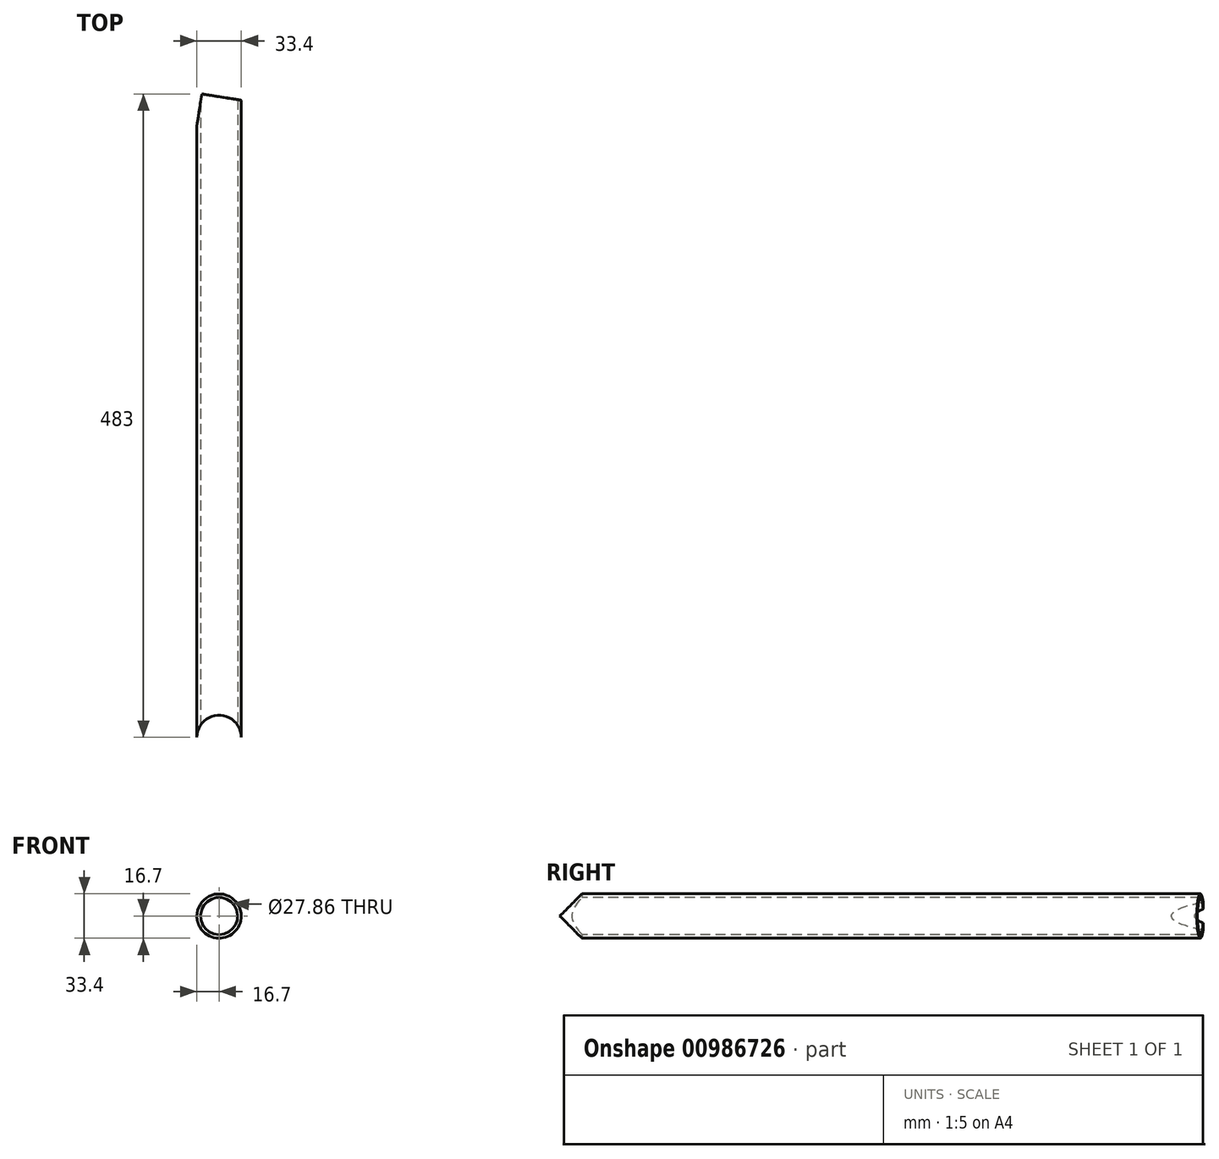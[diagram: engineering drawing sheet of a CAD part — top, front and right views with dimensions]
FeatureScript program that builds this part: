
annotation { "Feature Type Name" : "Feature", "Feature Type Description" : "" }
export const myFeature = defineFeature(function(context is Context, id is Id, definition is map)
    precondition{}
    {
        {
            var Q0;
            Q0=qCreatedBy(makeId("Right.planeOp"),FACE);
            var sketch = newSketch(context, id + "F0", { "sketchPlane" : qUnion([Q0])});
            skLineSegment(sketch, "E0", {"start": v(0, 0) * mm, "end": v(-483.6, 0) * mm});
            skPoint(sketch, "E1.visualSharp", {"position": v(-483.6, 0) * mm});
            skSolve(sketch);
        }
        {
            var Q0;
            Q0=qCreatedBy(makeId("Front.planeOp"),FACE);
            var sketch = newSketch(context, id + "F1", { "sketchPlane" : qUnion([Q0])});
            skCircle(sketch, "E2", {"center": v(0, 0) * mm, "radius": 16.7 * mm});
            skCircle(sketch, "E3.0", {"center": v(0, 0) * mm, "radius": 13.93 * mm});
            skSolve(sketch);
        }
        {
            var Q0;
            Q0=makeQuery(id+"F1.imprint","IMPRINT",FACE,{"disambiguationData":[TD([[makeQuery(id+"F1.imprint","IMPRINT",EDGE,{"derivedFrom":sQuery(id+"F1.wireOp",EDGE,"E2")}),1.0]])]});
            var Q1;
            Q1=sQuery(id+"F0.wireOp",EDGE,"E0");
            var Q2;
            Q2=sQuery(id+"F0.wireOp",EDGE,"E1.filletArc");
            var Q3;
            Q3=sQuery(id+"F0.wireOp",EDGE,"YA7wz6Jj-Of4G-qhnx-SV3L-edTmK6ZEOY0Y");
            sweep(context, id + "F2", {"profiles" : qUnion([Q0]), "path" : qUnion([Q1, Q2, Q3])});
        }
        {
            var Q0;
            Q0=qCreatedBy(makeId("Top.planeOp"),FACE);
            var sketch = newSketch(context, id + "F3", { "sketchPlane" : qUnion([Q0])});
            skLineSegment(sketch, "E4", {"start": v(0, 0) * mm, "end": v(29.63, -4.7) * mm});
            skLineSegment(sketch, "E5", {"start": v(0, 0) * mm, "end": v(16.7, 0) * mm});
            skLineSegment(sketch, "E6", {"start": v(16.7, 0) * mm, "end": v(16.7, -2.65) * mm});
            skLineSegment(sketch, "E7", {"start": v(0, 0) * mm, "end": v(2.57, 16.22) * mm});
            skLineSegment(sketch, "E8.MirrorCS", {"start": v(0, 0) * mm, "end": v(-29.63, 4.7) * mm});
            skLineSegment(sketch, "E9.MirrorCS", {"start": v(-15.88, 5.16) * mm, "end": v(-16.7, 2.65) * mm});
            skLineSegment(sketch, "E10", {"start": v(-16.7, 2.65) * mm, "end": v(-16.7, 0) * mm});
            skLineSegment(sketch, "E11", {"start": v(-16.7, 0) * mm, "end": v(17.86, -5.47) * mm});
            skLineSegment(sketch, "E12", {"start": v(-16.7, 0) * mm, "end": v(16.7, 0) * mm});
            skLineSegment(sketch, "E13", {"start": v(16.7, -5.47) * mm, "end": v(16.7, 0) * mm});
            skLineSegment(sketch, "E14", {"start": v(0, 0) * mm, "end": v(-16.7, 0) * mm});
            skLineSegment(sketch, "E15", {"start": v(-16.7, 0) * mm, "end": v(0, 0) * mm});
            skLineSegment(sketch, "E16", {"start": v(16.7, -5.3) * mm, "end": v(-12.93, -0.6) * mm});
            skLineSegment(sketch, "E17", {"start": v(-12.93, -0.6) * mm, "end": v(-19.43, -41.61) * mm});
            skLineSegment(sketch, "E18", {"start": v(-16.7, 0) * mm, "end": v(-16.7, -32.2) * mm});
            skSolve(sketch);
        }
        {
            var Q0;
            Q0 = qSketchRegion(id + "F3", true);
            extrude(context, id + "F4", {"entities" : qUnion([Q0]), "operationType" : NewBodyOperationType.REMOVE, "endBound" : BoundingType.THROUGH_ALL, "oppositeDirection" : true, "depth" : 25 * mm, "offsetDistance" : 25 * mm, "hasSecondDirection" : true, "secondDirectionBound" : BoundingType.THROUGH_ALL, "secondDirectionOppositeDirection" : false, "secondDirectionDepth" : 25 * mm});
        }
        {
            var Q0;
            Q0=qCreatedBy(makeId("Top.planeOp"),FACE);
            var sketch = newSketch(context, id + "F5", { "sketchPlane" : qUnion([Q0])});
            skCircle(sketch, "E19", {"center": v(0, -483.6) * mm, "radius": 16.7 * mm});
            skSolve(sketch);
        }
        {
            var Q0;
            Q0=makeQuery(id+"F5.imprint","IMPRINT",FACE,{"disambiguationData":[TD([[makeQuery(id+"F5.imprint","IMPRINT",EDGE,{"derivedFrom":sQuery(id+"F5.wireOp",EDGE,"E19")}),1.0]])]});
            extrude(context, id + "F6", {"entities" : qUnion([Q0]), "operationType" : NewBodyOperationType.REMOVE, "endBound" : BoundingType.THROUGH_ALL, "depth" : 25 * mm, "offsetDistance" : 25 * mm, "hasSecondDirection" : true, "secondDirectionBound" : BoundingType.THROUGH_ALL, "secondDirectionOppositeDirection" : true, "secondDirectionDepth" : 25 * mm});
        }
    });
